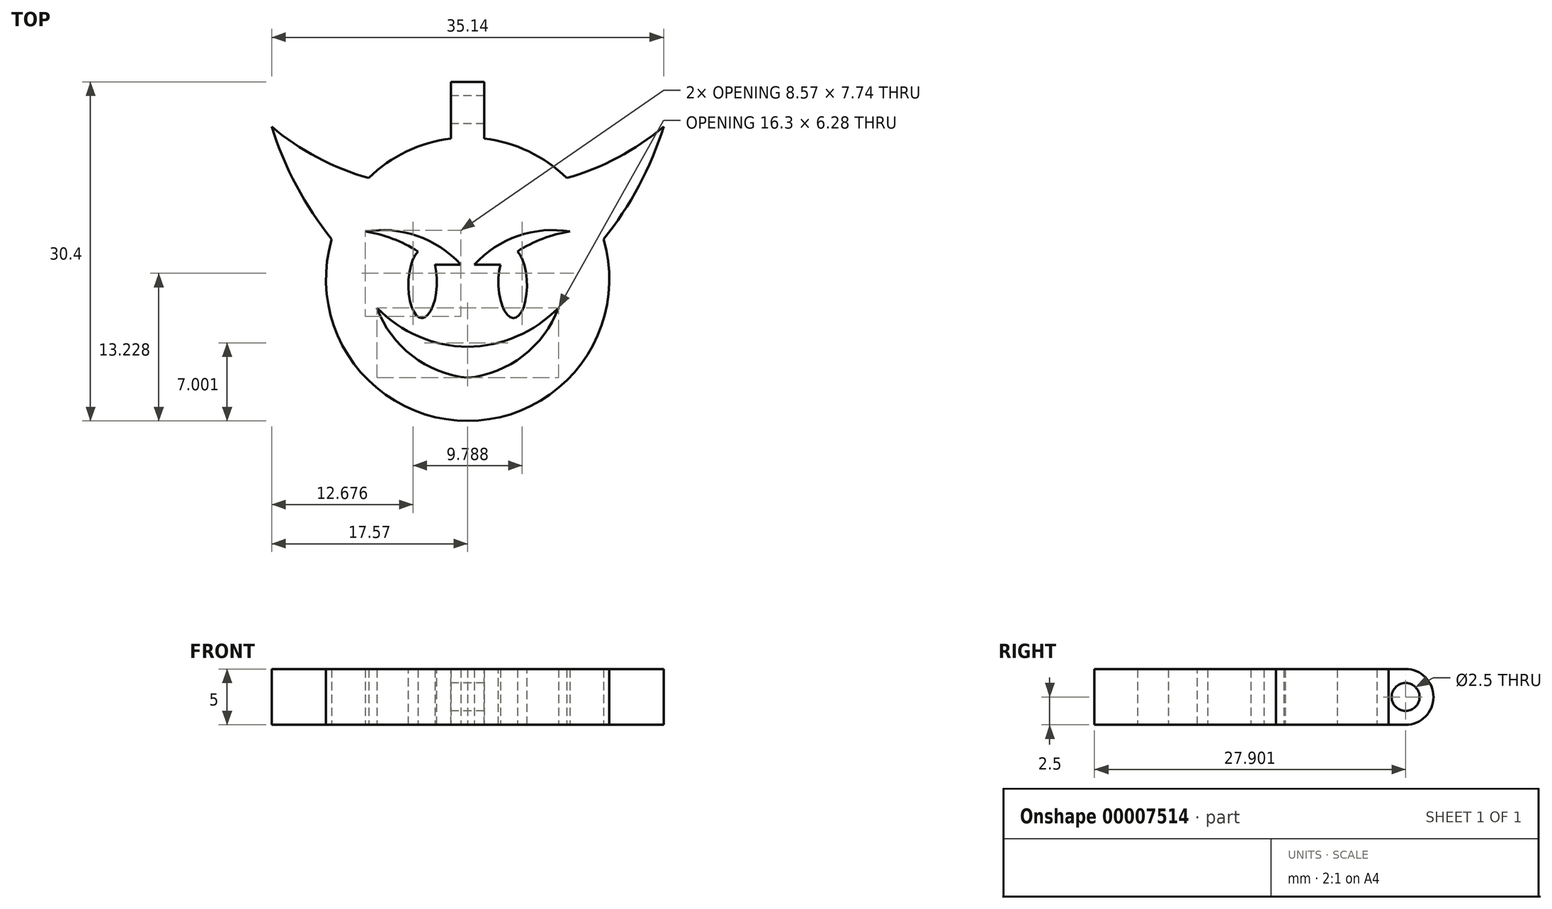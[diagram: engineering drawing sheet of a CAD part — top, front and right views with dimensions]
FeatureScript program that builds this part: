
annotation { "Feature Type Name" : "Feature", "Feature Type Description" : "" }
export const myFeature = defineFeature(function(context is Context, id is Id, definition is map)
    precondition{}
    {
        {
            var Q0;
            Q0=qCreatedBy(makeId("Top.planeOp"),FACE);
            var sketch = newSketch(context, id + "F0", { "sketchPlane" : qUnion([Q0])});
            skCircle(sketch, "E0", {"center": v(0, 0) * mm, "radius": 12.7 * mm});
            skLineSegment(sketch, "E1", {"start": v(0, -12.7) * mm, "end": v(0, 12.7) * mm, "construction": true});
            skLineSegment(sketch, "E2", {"start": v(-12.7, 0) * mm, "end": v(12.7, 0) * mm, "construction": true});
            skLineSegment(sketch, "E3", {"start": v(0, -0.38) * mm, "end": v(-4.04, -0.38) * mm, "construction": true});
            skLineSegment(sketch, "E4.0.MirrorCS", {"start": v(0, 11.94) * mm, "end": v(0, -13.46) * mm, "construction": true});
            skLineSegment(sketch, "E5.0.MirrorCS", {"start": v(0, -0.38) * mm, "end": v(4.04, -0.38) * mm, "construction": true});
            skEllipse(sketch, "E6", {"center": v(-4.04, -0.38) * mm, "majorRadius": 3.1 * mm, "minorRadius": 1.28 * mm, "majorAxis": v(-0.02, -1)});
            skEllipse(sketch, "E7.0.MirrorC", {"center": v(4.04, -0.38) * mm, "majorRadius": 3.1 * mm, "minorRadius": 1.28 * mm, "majorAxis": v(0.02, -1)});
            skArc(sketch, "E8", {"start": v(-17.57, 13.68) * mm, "mid": v(-13.47, 10.91) * mm, "end": v(-8.88, 9.08) * mm});
            skArc(sketch, "E9", {"start": v(-17.57, 13.68) * mm, "mid": v(-15.35, 8.38) * mm, "end": v(-12.18, 3.58) * mm});
            skArc(sketch, "E10.0.MirrorCS", {"start": v(17.57, 13.68) * mm, "mid": v(13.47, 10.91) * mm, "end": v(8.88, 9.08) * mm});
            skArc(sketch, "E11.0.MirrorCS", {"start": v(17.57, 13.68) * mm, "mid": v(15.35, 8.38) * mm, "end": v(12.18, 3.58) * mm});
            skArc(sketch, "E12", {"start": v(-0.6, 1.31) * mm, "mid": v(-4.52, 3.88) * mm, "end": v(-9.18, 4.28) * mm});
            skLineSegment(sketch, "E13", {"start": v(-0.6, 1.31) * mm, "end": v(-2.93, 1.31) * mm});
            skArc(sketch, "E14", {"start": v(-2.93, 1.31) * mm, "mid": v(-5.84, 3.26) * mm, "end": v(-9.18, 4.28) * mm});
            skArc(sketch, "E15.0.MirrorCS", {"start": v(0.6, 1.31) * mm, "mid": v(4.52, 3.88) * mm, "end": v(9.18, 4.28) * mm});
            skArc(sketch, "E16.0.MirrorCS", {"start": v(2.93, 1.31) * mm, "mid": v(5.84, 3.26) * mm, "end": v(9.18, 4.28) * mm});
            skLineSegment(sketch, "E17.0.MirrorCS", {"start": v(0.6, 1.31) * mm, "end": v(2.93, 1.31) * mm});
            skArc(sketch, "E18", {"start": v(-8.15, -2.56) * mm, "mid": v(-4.42, -5.12) * mm, "end": v(0, -6.07) * mm});
            skArc(sketch, "E19", {"start": v(-8.15, -2.56) * mm, "mid": v(-4.97, -6.86) * mm, "end": v(0, -8.84) * mm});
            skArc(sketch, "E20.0.MirrorCS", {"start": v(8.15, -2.56) * mm, "mid": v(4.42, -5.12) * mm, "end": v(0, -6.07) * mm});
            skArc(sketch, "E21.0.MirrorCS", {"start": v(8.15, -2.56) * mm, "mid": v(4.97, -6.86) * mm, "end": v(0, -8.84) * mm});
            skSolve(sketch);
        }
        {
            var Q0;
            Q0 = qSketchRegion(id + "F0", true);
            extrude(context, id + "F1", {"entities" : qUnion([Q0]), "depth" : 5 * mm});
        }
        {
            var Q0;
            Q0=qCreatedBy(makeId("Right.planeOp"),FACE);
            var sketch = newSketch(context, id + "F2", { "sketchPlane" : qUnion([Q0])});
            skLineSegment(sketch, "E22.bottom", {"start": v(8.75, 0) * mm, "end": v(15.2, 0) * mm});
            skLineSegment(sketch, "E22.top", {"start": v(8.75, 5) * mm, "end": v(15.2, 5) * mm});
            skLineSegment(sketch, "E22.left", {"start": v(8.75, 0) * mm, "end": v(8.75, 5) * mm});
            skLineSegment(sketch, "E22.right", {"start": v(15.2, 0) * mm, "end": v(15.2, 5) * mm, "construction": true});
            skLineSegment(sketch, "E23", {"start": v(8.75, 2.5) * mm, "end": v(15.2, 2.5) * mm, "construction": true});
            skArc(sketch, "E24", {"start": v(15.2, 0) * mm, "mid": v(17.7, 2.5) * mm, "end": v(15.2, 5) * mm});
            skLineSegment(sketch, "E25", {"start": v(17.7, 2.5) * mm, "end": v(12.7, 2.5) * mm, "construction": true});
            skPoint(sketch, "E26", {"position": v(11.03, 2.5) * mm});
            skLineSegment(sketch, "E27", {"start": v(12.7, 5) * mm, "end": v(12.7, 0) * mm, "construction": true});
            skCircle(sketch, "E28", {"center": v(15.2, 2.5) * mm, "radius": 1.25 * mm});
            skSolve(sketch);
        }
        {
            var Q0;
            Q0=makeQuery(id+"F2.imprint","IMPRINT",FACE,{"disambiguationData":[TD([[makeQuery(id+"F2.imprint","IMPRINT",EDGE,{"derivedFrom":sQuery(id+"F2.wireOp",EDGE,"E22.bottom")}),1.0]])]});
            extrude(context, id + "F3", {"entities" : qUnion([Q0]), "operationType" : NewBodyOperationType.ADD, "depth" : 3 * mm, "symmetric" : true});
        }
    });
